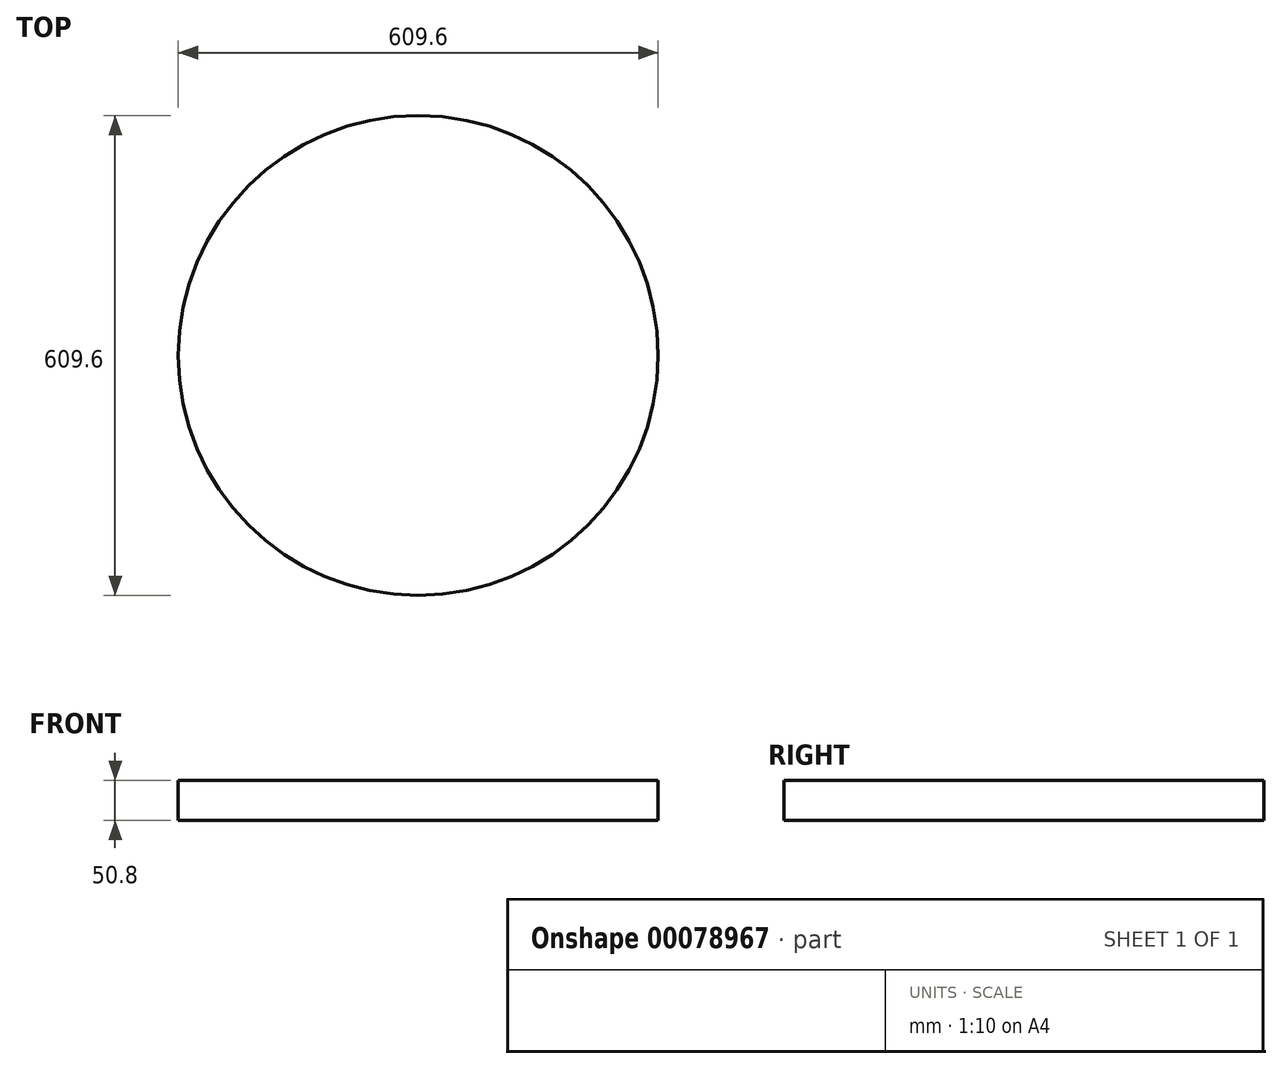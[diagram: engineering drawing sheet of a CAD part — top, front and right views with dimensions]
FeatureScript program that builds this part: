
annotation { "Feature Type Name" : "Feature", "Feature Type Description" : "" }
export const myFeature = defineFeature(function(context is Context, id is Id, definition is map)
    precondition{}
    {
        {
            var Q0;
            Q0=qCreatedBy(makeId("Top.planeOp"),FACE);
            var sketch = newSketch(context, id + "F0", { "sketchPlane" : qUnion([Q0])});
            skCircle(sketch, "E0", {"center": v(0, 0) * mm, "radius": 304.8 * mm});
            skSolve(sketch);
        }
        {
            var Q0;
            Q0=makeQuery(id+"F0.imprint","IMPRINT",FACE,{"disambiguationData":[TD([[makeQuery(id+"F0.imprint","IMPRINT",EDGE,{"derivedFrom":sQuery(id+"F0.wireOp",EDGE,"E0")}),1.0]])]});
            extrude(context, id + "F1", {"entities" : qUnion([Q0]), "depth" : 50.8 * mm});
        }
    });
